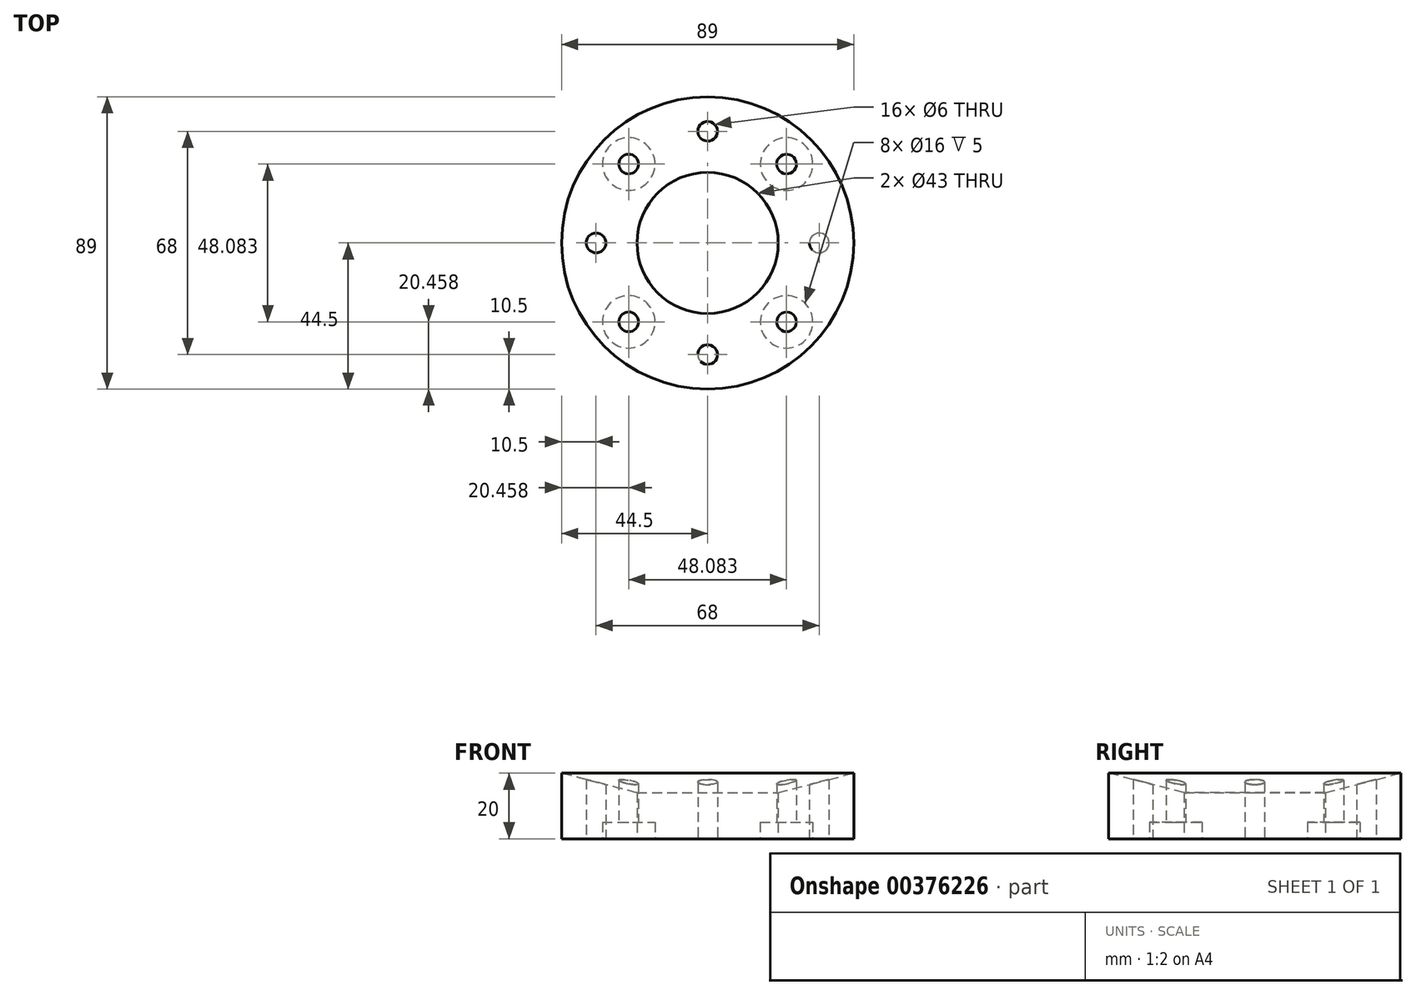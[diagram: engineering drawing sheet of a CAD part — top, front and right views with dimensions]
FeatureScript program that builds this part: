
annotation { "Feature Type Name" : "Feature", "Feature Type Description" : "" }
export const myFeature = defineFeature(function(context is Context, id is Id, definition is map)
    precondition{}
    {
        {
            var Q0;
            Q0=qCreatedBy(makeId("Front.planeOp"),FACE);
            var sketch = newSketch(context, id + "F0", { "sketchPlane" : qUnion([Q0])});
            skLineSegment(sketch, "E0", {"start": v(-21.5, 0) * mm, "end": v(-44.5, 0) * mm});
            skLineSegment(sketch, "E1", {"start": v(-44.5, 0) * mm, "end": v(-44.5, 20) * mm});
            skLineSegment(sketch, "E2", {"start": v(-21.5, 0) * mm, "end": v(-21.5, 14) * mm});
            skLineSegment(sketch, "E3", {"start": v(21.5, 0) * mm, "end": v(44.5, 0) * mm});
            skLineSegment(sketch, "E4", {"start": v(44.5, 0) * mm, "end": v(44.5, 20) * mm});
            skLineSegment(sketch, "E5", {"start": v(21.5, 0) * mm, "end": v(21.5, 14) * mm});
            skLineSegment(sketch, "E6", {"start": v(-21.5, 14) * mm, "end": v(-44.5, 20) * mm});
            skLineSegment(sketch, "E7", {"start": v(21.5, 14) * mm, "end": v(44.5, 20) * mm});
            skSolve(sketch);
        }
        {
            var Q0;
            Q0=qCreatedBy(makeId("Top.planeOp"),FACE);
            var sketch = newSketch(context, id + "F1", { "sketchPlane" : qUnion([Q0])});
            skCircle(sketch, "E8", {"center": v(0, 0) * mm, "radius": 44.5 * mm});
            skCircle(sketch, "E9", {"center": v(0, 0) * mm, "radius": 21.5 * mm});
            skSolve(sketch);
        }
        {
            var Q0;
            Q0 = qSketchRegion(id + "F0", true);
            var Q1;
            Q1=sQuery(id+"F1.wireOp",EDGE,"E9");
            revolve(context, id + "F2", {"entities" : qUnion([Q0]), "axis" : qUnion([Q1]), "revolveType" : RevolveType.FULL});
        }
        {
            var Q0;
            Q0=qCreatedBy(makeId("Top.planeOp"),FACE);
            var sketch = newSketch(context, id + "F3", { "sketchPlane" : qUnion([Q0])});
            skCircle(sketch, "E10", {"center": v(-34, 0) * mm, "radius": 3 * mm});
            skCircle(sketch, "E11.1.0", {"center": v(-24.04, -24.04) * mm, "radius": 3 * mm});
            skCircle(sketch, "E11.2.0", {"center": v(0, -34) * mm, "radius": 3 * mm});
            skCircle(sketch, "E11.3.0", {"center": v(24.04, -24.04) * mm, "radius": 3 * mm});
            skCircle(sketch, "E11.4.0", {"center": v(34, 0) * mm, "radius": 3 * mm});
            skCircle(sketch, "E11.5.0", {"center": v(24.04, 24.04) * mm, "radius": 3 * mm});
            skCircle(sketch, "E11.6.0", {"center": v(0, 34) * mm, "radius": 3 * mm});
            skCircle(sketch, "E11.7.0", {"center": v(-24.04, 24.04) * mm, "radius": 3 * mm});
            skPoint(sketch, "E11.center", {"position": v(0, 0) * mm});
            skSolve(sketch);
        }
        {
            var Q0;
            Q0=sQuery(id+"F3.wireOp",VERTEX,"E10.center");
            var Q1;
            Q1=sQuery(id+"F3.wireOp",VERTEX,"E11.2.0.center");
            var Q2;
            Q2=sQuery(id+"F3.wireOp",VERTEX,"E11.4.0.center");
            var Q3;
            Q3=sQuery(id+"F3.wireOp",VERTEX,"E11.6.0.center");
            var Q4;
            Q4=makeQuery(id+"F2.opRevolve","SWEPT_BODY",BODY,{"disambiguationData":[OSD([sQuery(id+"F0.wireOp",EDGE,"E0"),sQuery(id+"F0.wireOp",EDGE,"E1"),sQuery(id+"F0.wireOp",EDGE,"E2"),sQuery(id+"F0.wireOp",EDGE,"E6")])]});
            var Q5;
            Q5=makeQuery(id+"F2.opRevolve","SWEPT_BODY",BODY,{"disambiguationData":[OSD([sQuery(id+"F0.wireOp",EDGE,"E3"),sQuery(id+"F0.wireOp",EDGE,"E4"),sQuery(id+"F0.wireOp",EDGE,"E5"),sQuery(id+"F0.wireOp",EDGE,"E7")])]});
            hole(context, id + "F4", {"style" : HoleStyle.SIMPLE, "endStyle" : HoleEndStyle.THROUGH, "oppositeDirection" : true, "holeDiameter" : 6 * mm, "isTappedThrough" : true, "tappedDepth" : 12 * mm, "tapClearance" : 3, "locations" : qUnion([Q0, Q1, Q2, Q3]), "scope" : qUnion([Q4, Q5])});
        }
        {
            var Q0;
            Q0=sQuery(id+"F3.wireOp",VERTEX,"E11.1.0.center");
            var Q1;
            Q1=sQuery(id+"F3.wireOp",VERTEX,"E11.3.0.center");
            var Q2;
            Q2=sQuery(id+"F3.wireOp",VERTEX,"E11.5.0.center");
            var Q3;
            Q3=sQuery(id+"F3.wireOp",VERTEX,"E11.7.0.center");
            var Q4;
            Q4=makeQuery(id+"F2.opRevolve","SWEPT_BODY",BODY,{"disambiguationData":[OSD([sQuery(id+"F0.wireOp",EDGE,"E0"),sQuery(id+"F0.wireOp",EDGE,"E1"),sQuery(id+"F0.wireOp",EDGE,"E2"),sQuery(id+"F0.wireOp",EDGE,"E6")])]});
            var Q5;
            Q5=makeQuery(id+"F2.opRevolve","SWEPT_BODY",BODY,{"disambiguationData":[OSD([sQuery(id+"F0.wireOp",EDGE,"E3"),sQuery(id+"F0.wireOp",EDGE,"E4"),sQuery(id+"F0.wireOp",EDGE,"E5"),sQuery(id+"F0.wireOp",EDGE,"E7")])]});
            hole(context, id + "F5", {"style" : HoleStyle.C_BORE, "endStyle" : HoleEndStyle.THROUGH, "oppositeDirection" : true, "holeDiameter" : 6 * mm, "cBoreDiameter" : 16 * mm, "cBoreDepth" : 5 * mm, "isTappedThrough" : true, "tappedDepth" : 12 * mm, "tapClearance" : 3, "locations" : qUnion([Q0, Q1, Q2, Q3]), "scope" : qUnion([Q4, Q5])});
        }
    });
